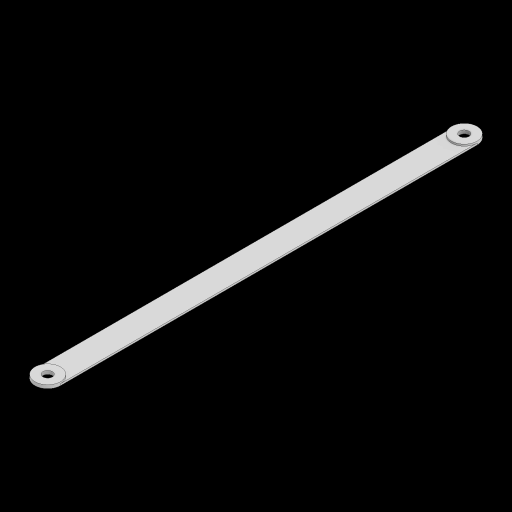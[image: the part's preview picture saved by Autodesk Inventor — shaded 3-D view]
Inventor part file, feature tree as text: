
AUTODESK INVENTOR PART (.ipt)
format: ipt  version: 2023 (Build 270158000, 158)  size: 94,720 bytes
history: native  units: mm
features: extrude x2, sketch x1
ambient origin geometry x8: Origin, YZ Plane, XZ Plane, XY Plane, X Axis, Y Axis, Z Axis, Center Point
bodies: Body1 (feature_tree)
feature tree (3):
  sketch  "Sketch1"  dims[d0=5.5mm d1=15.0mm d14=5.5mm d15=15.0mm d16=1.0mm d17=0.0mm d18=2.0mm d19=0.0mm d20=259.423mm]
  extrude  "Extrusion4"  Depth=15.0mm
  extrude  "Extrusion5"  Depth=2.0mm
